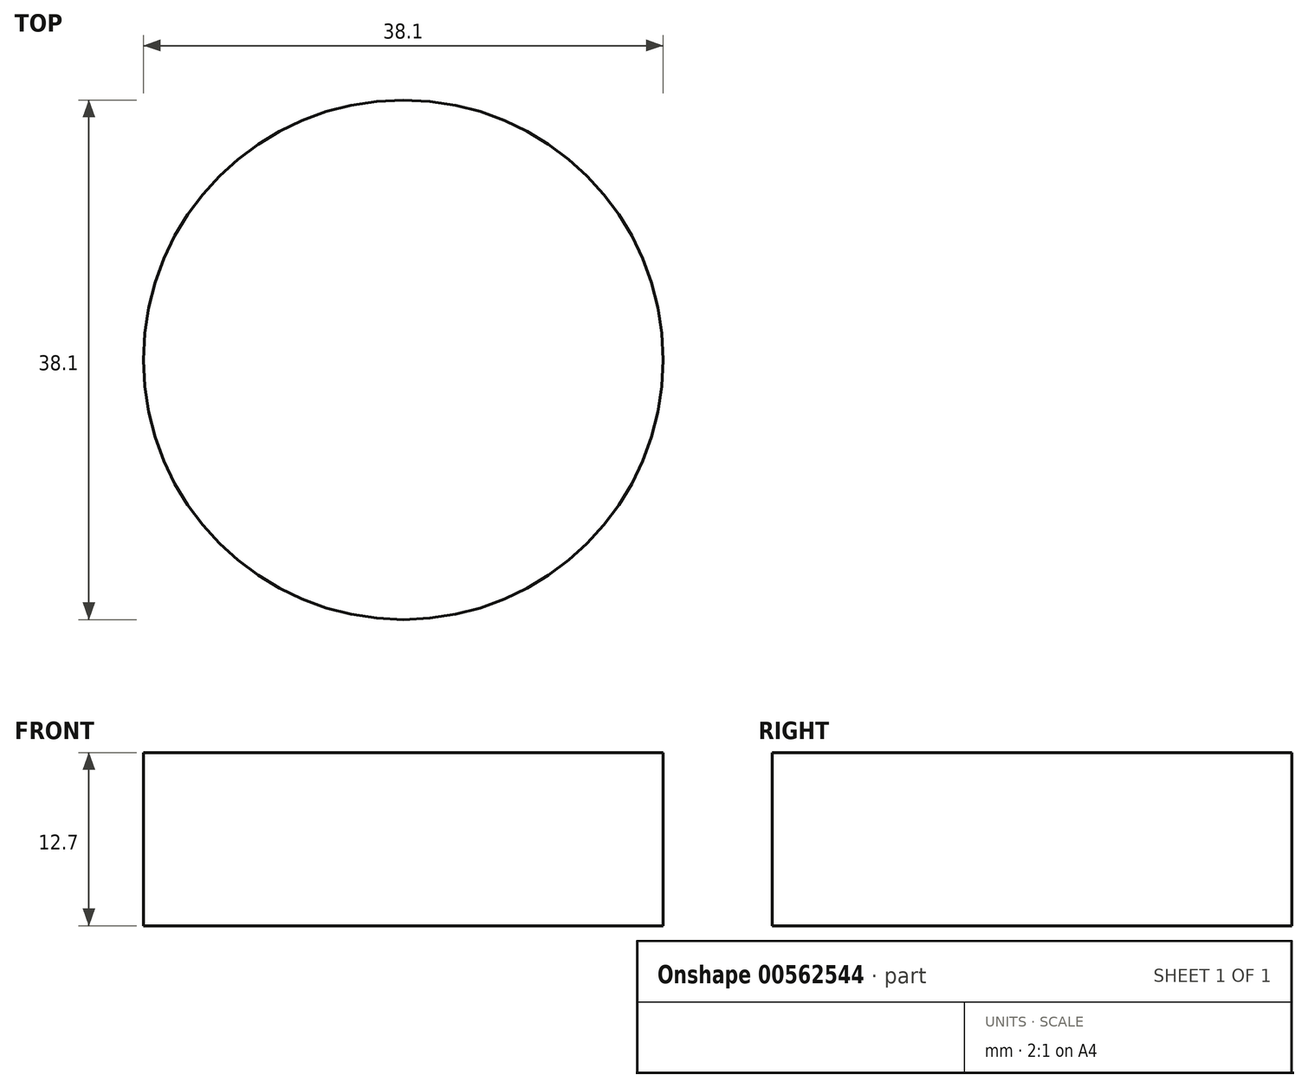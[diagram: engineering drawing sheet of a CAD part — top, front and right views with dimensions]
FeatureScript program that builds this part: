
annotation { "Feature Type Name" : "Feature", "Feature Type Description" : "" }
export const myFeature = defineFeature(function(context is Context, id is Id, definition is map)
    precondition{}
    {
        {
            var Q0;
            Q0=qCreatedBy(makeId("Top.planeOp"),FACE);
            var sketch = newSketch(context, id + "F0", { "sketchPlane" : qUnion([Q0])});
            skCircle(sketch, "E0", {"center": v(0, 0) * mm, "radius": 19.05 * mm});
            skSolve(sketch);
        }
        {
            var Q0;
            Q0=makeQuery(id+"F0.imprint","IMPRINT",FACE,{"disambiguationData":[TD([[makeQuery(id+"F0.imprint","IMPRINT",EDGE,{"derivedFrom":sQuery(id+"F0.wireOp",EDGE,"E0")}),1.0]])]});
            extrude(context, id + "F1", {"entities" : qUnion([Q0]), "depth" : 12.7 * mm, "offsetDistance" : 25.4 * mm});
        }
    });
